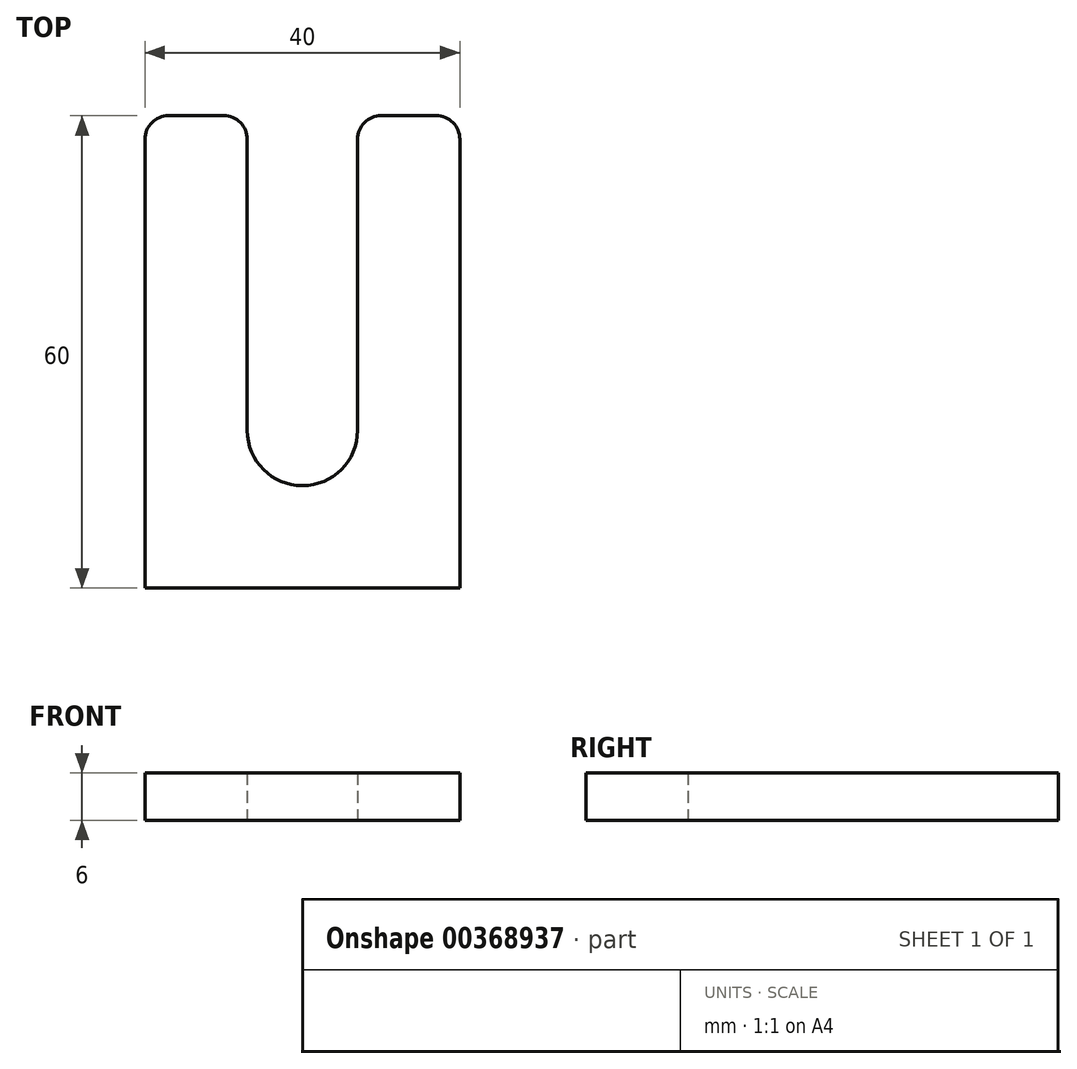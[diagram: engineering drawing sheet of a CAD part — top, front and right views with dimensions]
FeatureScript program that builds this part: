
annotation { "Feature Type Name" : "Feature", "Feature Type Description" : "" }
export const myFeature = defineFeature(function(context is Context, id is Id, definition is map)
    precondition{}
    {
        {
            var Q0;
            Q0=qCreatedBy(makeId("Top.planeOp"),FACE);
            var sketch = newSketch(context, id + "F0", { "sketchPlane" : qUnion([Q0])});
            skLineSegment(sketch, "E0", {"start": v(22.66, -14.77) * mm, "end": v(-17.34, -14.77) * mm});
            skLineSegment(sketch, "E1", {"start": v(-17.34, -14.77) * mm, "end": v(-17.34, 42.23) * mm});
            skLineSegment(sketch, "E2", {"start": v(-14.34, 45.23) * mm, "end": v(-7.34, 45.23) * mm});
            skLineSegment(sketch, "E3", {"start": v(-4.34, 42.23) * mm, "end": v(-4.34, 5.23) * mm});
            skLineSegment(sketch, "E4", {"start": v(2.66, -0.22) * mm, "end": v(2.7, -0.22) * mm});
            skLineSegment(sketch, "E5", {"start": v(9.66, 5.23) * mm, "end": v(9.66, 42.23) * mm});
            skLineSegment(sketch, "E6", {"start": v(12.66, 45.23) * mm, "end": v(19.66, 45.23) * mm});
            skLineSegment(sketch, "E7", {"start": v(22.66, 42.23) * mm, "end": v(22.66, -14.77) * mm});
            skPoint(sketch, "E8.second.point", {"position": v(2.66, -0.22) * mm});
            skArc(sketch, "E9", {"start": v(-4.34, 5.23) * mm, "mid": v(2.66, -1.77) * mm, "end": v(9.66, 5.23) * mm});
            skPoint(sketch, "E10.visualSharp", {"position": v(22.66, 45.23) * mm});
            skArc(sketch, "E10.filletArc", {"start": v(22.66, 42.23) * mm, "mid": v(21.78, 44.35) * mm, "end": v(19.66, 45.23) * mm});
            skPoint(sketch, "E11.visualSharp", {"position": v(9.66, 45.23) * mm});
            skArc(sketch, "E11.filletArc", {"start": v(12.66, 45.23) * mm, "mid": v(10.54, 44.35) * mm, "end": v(9.66, 42.23) * mm});
            skPoint(sketch, "E12.visualSharp", {"position": v(-4.34, 45.23) * mm});
            skArc(sketch, "E12.filletArc", {"start": v(-4.34, 42.23) * mm, "mid": v(-5.22, 44.35) * mm, "end": v(-7.34, 45.23) * mm});
            skPoint(sketch, "E13.visualSharp", {"position": v(-17.34, 45.23) * mm});
            skArc(sketch, "E13.filletArc", {"start": v(-14.34, 45.23) * mm, "mid": v(-16.46, 44.35) * mm, "end": v(-17.34, 42.23) * mm});
            skSolve(sketch);
        }
        {
            var Q0;
            Q0=makeQuery(id+"F0.imprint","IMPRINT",FACE,{"disambiguationData":[TD([[makeQuery(id+"F0.imprint","IMPRINT",EDGE,{"derivedFrom":sQuery(id+"F0.wireOp",EDGE,"E0")}),-1.0]])]});
            extrude(context, id + "F1", {"entities" : qUnion([Q0]), "depth" : 6 * mm});
        }
    });
